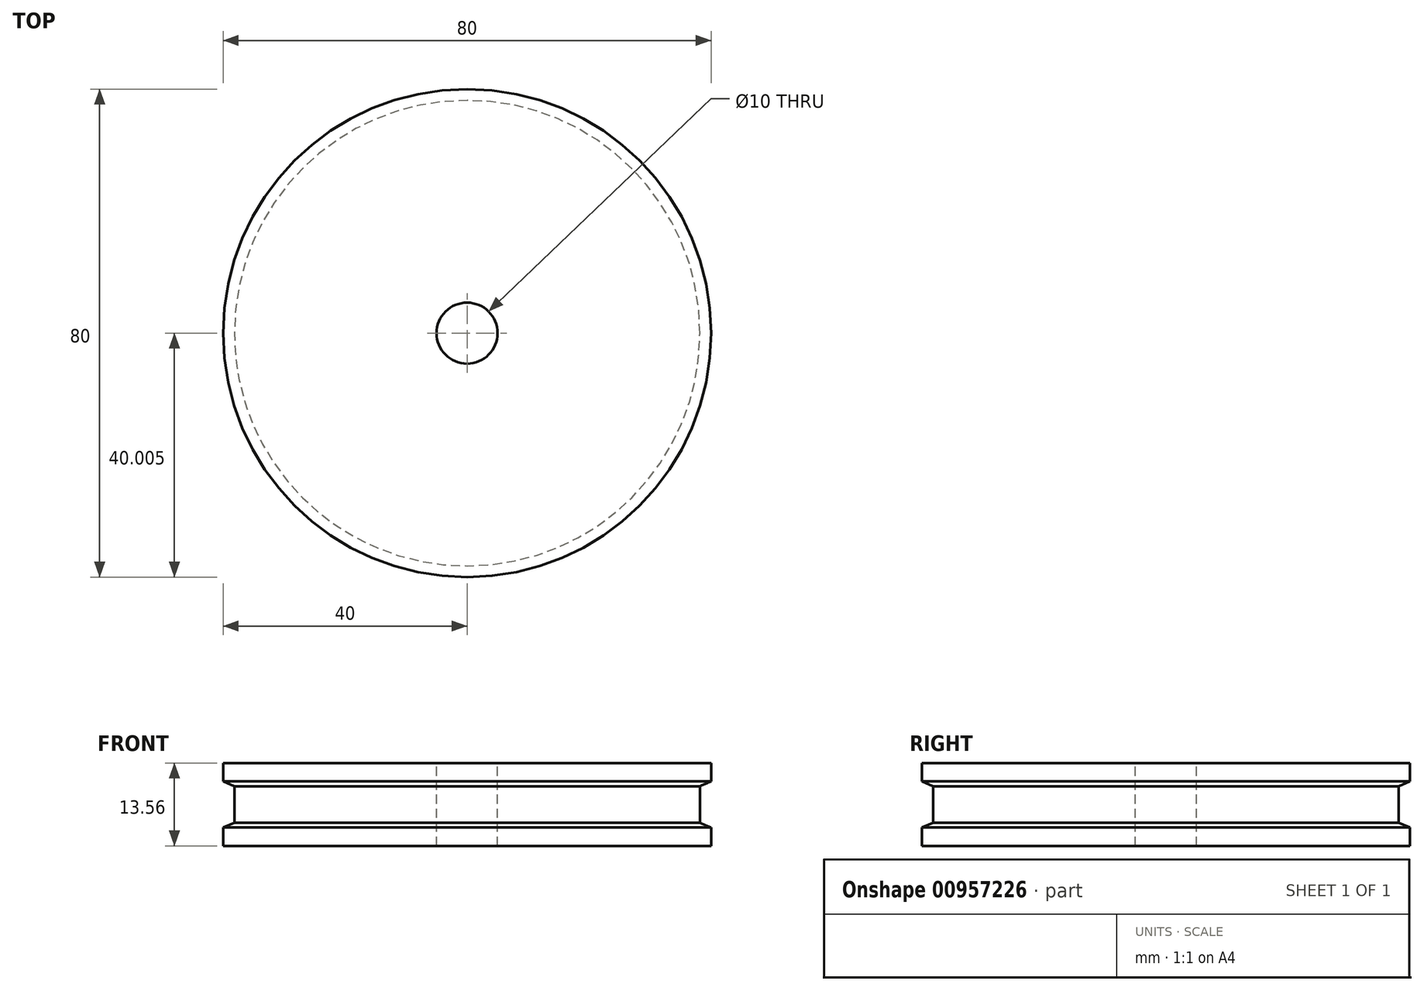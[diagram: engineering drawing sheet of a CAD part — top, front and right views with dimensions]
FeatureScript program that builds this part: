
annotation { "Feature Type Name" : "Feature", "Feature Type Description" : "" }
export const myFeature = defineFeature(function(context is Context, id is Id, definition is map)
    precondition{}
    {
        {
            var Q0;
            Q0=qCreatedBy(makeId("Right.planeOp"),FACE);
            var sketch = newSketch(context, id + "F0", { "sketchPlane" : qUnion([Q0])});
            skLineSegment(sketch, "E0.bottom", {"start": v(-86.65, 29.3) * mm, "end": v(-51.65, 29.3) * mm});
            skLineSegment(sketch, "E0.top", {"start": v(-86.65, 15.74) * mm, "end": v(-51.65, 15.74) * mm});
            skLineSegment(sketch, "E0.right", {"start": v(-51.65, 29.3) * mm, "end": v(-51.65, 15.74) * mm});
            skLineSegment(sketch, "E1", {"start": v(-86.65, 29.3) * mm, "end": v(-86.65, 26.3) * mm});
            skLineSegment(sketch, "E2", {"start": v(-86.65, 26.3) * mm, "end": v(-84.8, 25.52) * mm});
            skLineSegment(sketch, "E3", {"start": v(-84.8, 25.52) * mm, "end": v(-84.8, 19.52) * mm});
            skLineSegment(sketch, "E4", {"start": v(-84.8, 19.52) * mm, "end": v(-86.65, 18.74) * mm});
            skLineSegment(sketch, "E5", {"start": v(-86.65, 18.74) * mm, "end": v(-86.65, 15.74) * mm});
            skLineSegment(sketch, "E6", {"start": v(-46.65, 43.53) * mm, "end": v(-46.65, 6.82) * mm, "construction": true});
            skSolve(sketch);
        }
        {
            var Q0;
            Q0=makeQuery(id+"F0.imprint","IMPRINT",FACE,{"disambiguationData":[TD([[makeQuery(id+"F0.imprint","IMPRINT",EDGE,{"derivedFrom":sQuery(id+"F0.wireOp",EDGE,"E0.bottom")}),-1.0]])]});
            var Q1;
            Q1=sQuery(id+"F0.wireOp",EDGE,"E6");
            revolve(context, id + "F1", {"surfaceOperationType" : NewSurfaceOperationType.NEW, "entities" : qUnion([Q0]), "axis" : qUnion([Q1]), "revolveType" : RevolveType.FULL});
        }
    });
